# Revit family: ledfloodoly-p_re700-1000w-730-as-lum_709000084900
name_source: partatom
category: Lighting Fixtures
units: mm (PartAtom-declared; Revit-internal decimal feet)

## family parameters
Cut with Voids When Loaded = No
Host = Face
Light Source = No
Part Type = Normal
Room Calculation Point = No
Round Connector Dimension = Use Diameter
Shared = No

## types (1)
- LEDFloodOly-P Re700-1000W-730-AS-LUM (1 x LED, 140000 lm, 3000)
    Apparent Load = 1000 VA
    Approval mark = CE, ENEC
    CIE Flux Codes = 57 94 100 100 100
    Color Rendering = 70
    Color Temperature = 3000
    Control Gear = Electronic ballast
    Default Elevation = 1800 mm
    Description = Professional luminaire with die-cast aluminium body for sports and area lighting. Flexible driver mounting methods. Robust design: full IP66 and IK08 protection, including safety cable. Equipped with DALI dimming for further energy saving. Equipped with b
    Frequency = 60 Hz
    Height = 356 mm
    Lamp = 1 x LED
    Lamp Light Flux = 140000 lm
    Lamp count = 1
    Length = 701 mm
    Luminous efficacy = 140 lm/W
    Manufacturer = OPPLE
    ModVariant = No
    Model = 709000084900
    Mounting Place = Ceiling
    Mounting Type = Surface mounted
    Number of Poles = 1
    OnlyDefault = Yes
    Power Factor = 1
    Product Name = LEDFloodOly-P Re700-1000W-730-AS-LUM
    Product group = Filament A60
    ProductGroupID = 310
    Protection Class = Protection class I
    Protection Degree = IP 66
    RLX_Detail_Level = 1
    RlxData = <blob elided: 236957 chars, md5=54b5cc7d>
    Socket = socket
    Standby Power = 0 W
    System Light Flux = 140000 lm
    System Power = 1000 W
    Type Comments = Product without accessories
    Type Image = web_fl_olympus_re700_v4.jpg
    URL = http://relux.com
    VarID = ---
    Voltage = 230 V
    Voltage Range = 220-240 V
    Weight = 0.00 kg
    Width = 612 mm

## geometry (parser evidence)
native form markers: Blend x4, Sweep x12
no freeform markers — native parametric forms only
